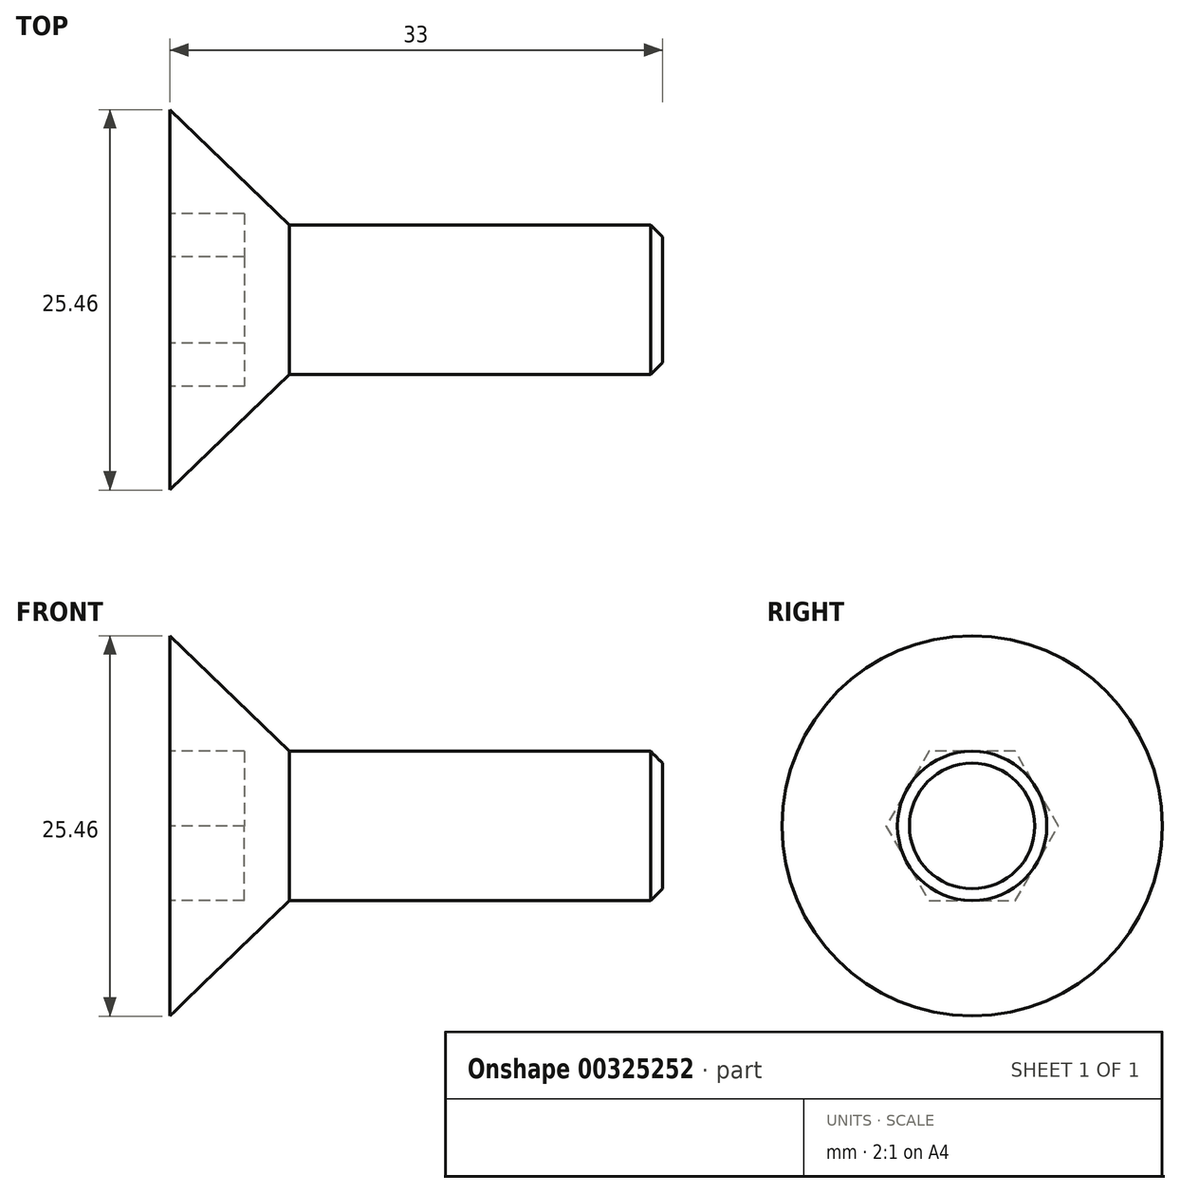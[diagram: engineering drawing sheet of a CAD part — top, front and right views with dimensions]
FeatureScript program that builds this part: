
annotation { "Feature Type Name" : "Feature", "Feature Type Description" : "" }
export const myFeature = defineFeature(function(context is Context, id is Id, definition is map)
    precondition{}
    {
        {
            var Q0;
            Q0=qCreatedBy(makeId("Front.planeOp"),FACE);
            var sketch = newSketch(context, id + "F0", { "sketchPlane" : qUnion([Q0])});
            skLineSegment(sketch, "E0", {"start": v(0, 0) * mm, "end": v(0, 12.73) * mm});
            skLineSegment(sketch, "E1", {"start": v(0, 12.73) * mm, "end": v(8, 5) * mm});
            skLineSegment(sketch, "E2", {"start": v(8, 5) * mm, "end": v(33, 5) * mm});
            skLineSegment(sketch, "E3", {"start": v(33, 5) * mm, "end": v(33, 0) * mm});
            skLineSegment(sketch, "E4", {"start": v(33, 0) * mm, "end": v(0, 0) * mm});
            skLineSegment(sketch, "E5", {"start": v(33, 0) * mm, "end": v(38.54, 0) * mm, "construction": true});
            skSolve(sketch);
        }
        {
            var Q0;
            Q0 = qSketchRegion(id + "F0", true);
            var Q1;
            Q1=sQuery(id+"F0.wireOp",EDGE,"E4");
            revolve(context, id + "F1", {"entities" : qUnion([Q0]), "axis" : qUnion([Q1]), "revolveType" : RevolveType.FULL});
        }
        {
            var Q0;
            Q0=makeQuery(id+"F1.opRevolve","SWEPT_FACE",FACE,{"disambiguationData":[OSD([sQuery(id+"F0.wireOp",EDGE,"E0")])]});
            var sketch = newSketch(context, id + "F2", { "sketchPlane" : qUnion([Q0])});
            skCircle(sketch, "E6.cCircle", {"center": v(0, 0) * mm, "radius": 5 * mm, "construction": true});
            skLineSegment(sketch, "E6.0", {"start": v(2.89, 5) * mm, "end": v(5.77, 0) * mm});
            skLineSegment(sketch, "E6.1", {"start": v(5.77, 0) * mm, "end": v(2.89, -5) * mm});
            skLineSegment(sketch, "E6.2", {"start": v(2.89, -5) * mm, "end": v(-2.89, -5) * mm});
            skLineSegment(sketch, "E6.3", {"start": v(-2.89, -5) * mm, "end": v(-5.77, 0) * mm});
            skLineSegment(sketch, "E6.4", {"start": v(-5.77, 0) * mm, "end": v(-2.89, 5) * mm});
            skLineSegment(sketch, "E6.5", {"start": v(-2.89, 5) * mm, "end": v(2.89, 5) * mm});
            skPoint(sketch, "E6.0.midPoint", {"position": v(4.33, 2.5) * mm});
            skSolve(sketch);
        }
        {
            var Q0;
            Q0=makeQuery(id+"F2.imprint","IMPRINT",FACE,{"disambiguationData":[TD([[makeQuery(id+"F2.imprint","IMPRINT",EDGE,{"derivedFrom":sQuery(id+"F2.wireOp",EDGE,"E6.0")}),-1.0]])]});
            extrude(context, id + "F3", {"entities" : qUnion([Q0]), "operationType" : NewBodyOperationType.REMOVE, "oppositeDirection" : true, "depth" : 5 * mm});
        }
        {
            var Q0;
            Q0=makeQuery(id+"F1.opRevolve","SWEPT_FACE",FACE,{"disambiguationData":[OSD([sQuery(id+"F0.wireOp",EDGE,"E3")])]});
            chamfer(context, id + "F4", {"entities" : qUnion([Q0]), "width" : 0.8 * mm, "tangentPropagation" : true});
        }
    });
